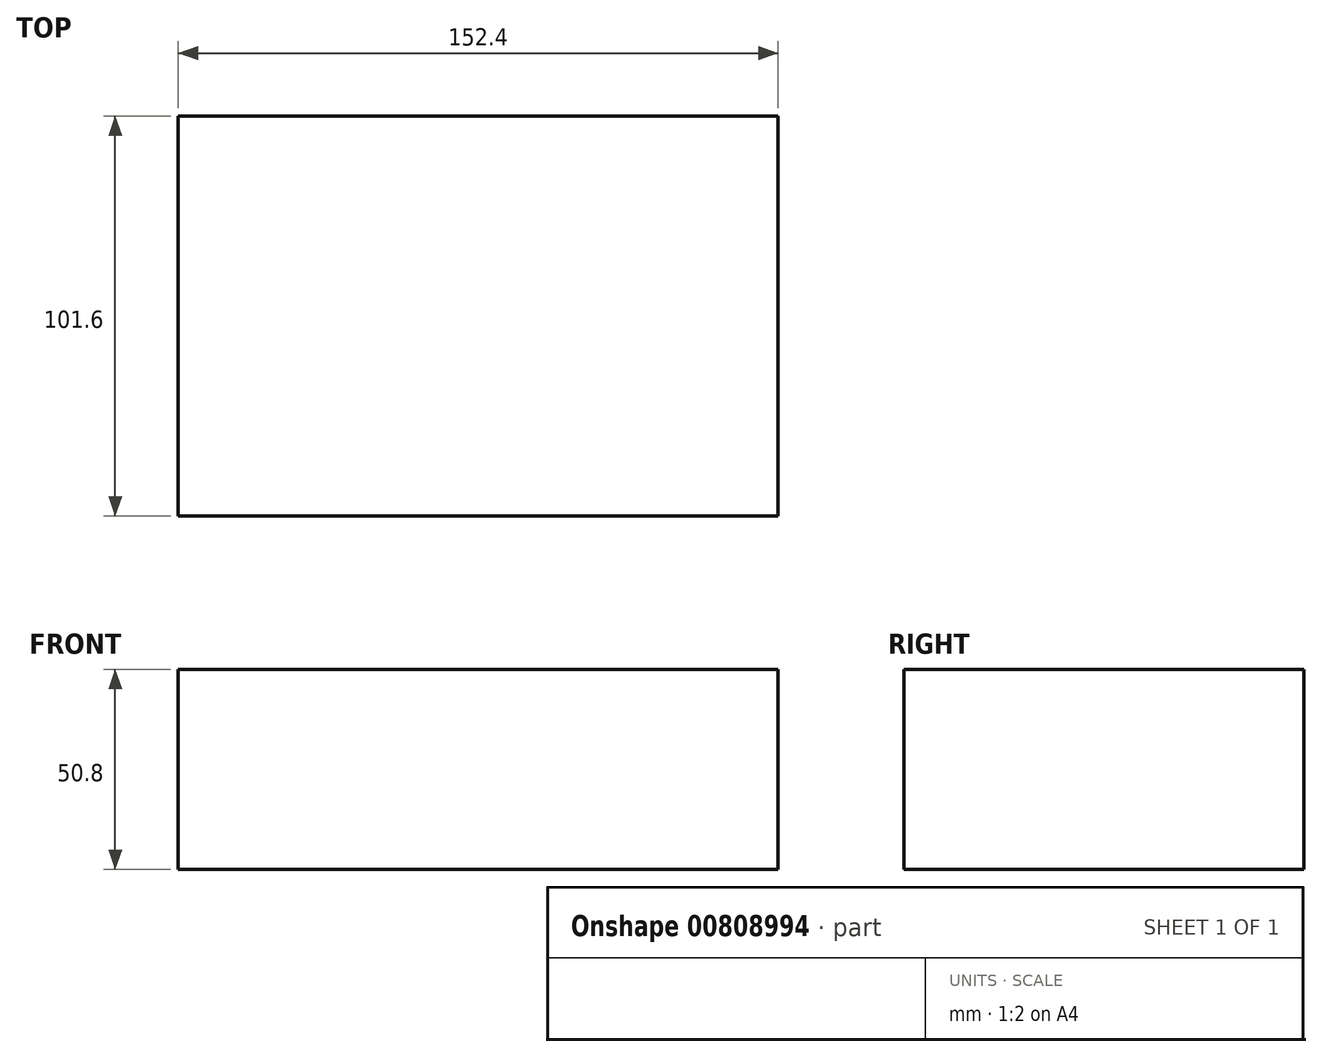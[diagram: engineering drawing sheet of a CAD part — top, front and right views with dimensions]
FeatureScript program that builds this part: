
annotation { "Feature Type Name" : "Feature", "Feature Type Description" : "" }
export const myFeature = defineFeature(function(context is Context, id is Id, definition is map)
    precondition{}
    {
        {
            var Q0;
            Q0=qCreatedBy(makeId("Top.planeOp"),FACE);
            var sketch = newSketch(context, id + "F0", { "sketchPlane" : qUnion([Q0])});
            skLineSegment(sketch, "E0.bottom", {"start": v(76.2, -50.8) * mm, "end": v(-76.2, -50.8) * mm});
            skLineSegment(sketch, "E0.top", {"start": v(76.2, 50.8) * mm, "end": v(-76.2, 50.8) * mm});
            skLineSegment(sketch, "E0.left", {"start": v(76.2, -50.8) * mm, "end": v(76.2, 50.8) * mm});
            skLineSegment(sketch, "E0.right", {"start": v(-76.2, -50.8) * mm, "end": v(-76.2, 50.8) * mm});
            skPoint(sketch, "E0.middle", {"position": v(0, 0) * mm});
            skSolve(sketch);
        }
        {
            var Q0;
            Q0=makeQuery(id+"F0.imprint","IMPRINT",FACE,{"disambiguationData":[TD([[makeQuery(id+"F0.imprint","IMPRINT",EDGE,{"derivedFrom":sQuery(id+"F0.wireOp",EDGE,"E0.bottom")}),-1.0]])]});
            extrude(context, id + "F1", {"entities" : qUnion([Q0]), "depth" : 50.8 * mm, "offsetDistance" : 25.4 * mm});
        }
    });
